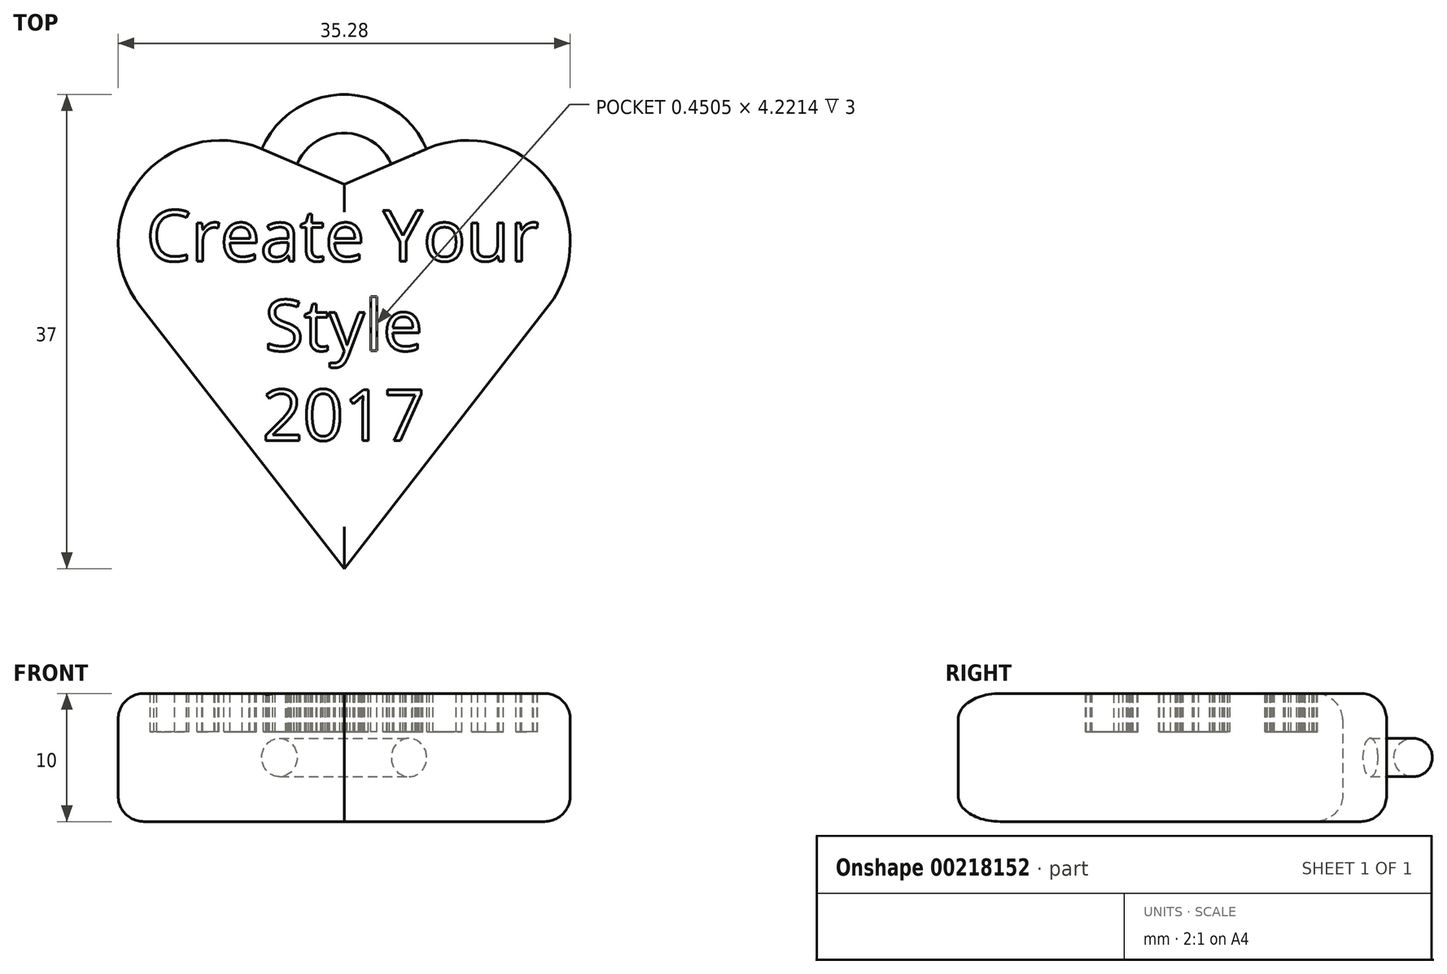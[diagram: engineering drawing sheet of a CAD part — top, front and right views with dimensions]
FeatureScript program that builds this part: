
annotation { "Feature Type Name" : "Feature", "Feature Type Description" : "" }
export const myFeature = defineFeature(function(context is Context, id is Id, definition is map)
    precondition{}
    {
        {
            var Q0;
            Q0=qCreatedBy(makeId("Top.planeOp"),FACE);
            var sketch = newSketch(context, id + "F0", { "sketchPlane" : qUnion([Q0])});
            skLineSegment(sketch, "E0", {"start": v(0, 0) * mm, "end": v(35, 45) * mm});
            skLineSegment(sketch, "E1", {"start": v(35, 45) * mm, "end": v(0, 30) * mm});
            skLineSegment(sketch, "E2.MirrorCS", {"start": v(-35, 45) * mm, "end": v(0, 30) * mm});
            skLineSegment(sketch, "E3.MirrorCS", {"start": v(0, 0) * mm, "end": v(-35, 45) * mm});
            skSolve(sketch);
        }
        {
            var Q0;
            Q0 = qSketchRegion(id + "F0", true);
            extrude(context, id + "F1", {"entities" : qUnion([Q0]), "depth" : 10 * mm, "symmetric" : true});
        }
        {
            var Q0;
            Q0=makeQuery(id+"F1.opExtrude","SWEPT_EDGE",EDGE,{"disambiguationData":[OSD([sQuery(id+"F0.wireOp",EDGE,"E2.MirrorCS"),sQuery(id+"F0.wireOp",EDGE,"E3.MirrorCS")])]});
            var Q1;
            Q1=makeQuery(id+"F1.opExtrude","SWEPT_EDGE",EDGE,{"disambiguationData":[OSD([sQuery(id+"F0.wireOp",EDGE,"E0"),sQuery(id+"F0.wireOp",EDGE,"E1")])]});
            fillet(context, id + "F2", {"entities" : qUnion([Q0, Q1]), "radius" : 8 * mm, "tangentPropagation" : true, "allowEdgeOverflow" : false});
        }
        {
            var Q0;
            Q0=qCreatedBy(makeId("Top.planeOp"),FACE);
            var sketch = newSketch(context, id + "F3", { "sketchPlane" : qUnion([Q0])});
            skCircle(sketch, "E4", {"center": v(0, 30) * mm, "radius": 7 * mm});
            skCircle(sketch, "E5", {"center": v(0, 30) * mm, "radius": 4 * mm});
            skSolve(sketch);
        }
        {
            var Q0;
            Q0=makeQuery(id+"F3.imprint","IMPRINT",FACE,{"disambiguationData":[TD([[makeQuery(id+"F3.imprint","IMPRINT",EDGE,{"derivedFrom":sQuery(id+"F3.wireOp",EDGE,"E4")}),1.0]])]});
            extrude(context, id + "F4", {"entities" : qUnion([Q0]), "operationType" : NewBodyOperationType.ADD, "depth" : 3 * mm, "symmetric" : true});
        }
        {
            var Q0;
            Q0=makeQuery(id+"F4.opExtrude","CAP_EDGE",EDGE,{"disambiguationData":[OSD([sQuery(id+"F3.wireOp",EDGE,"E4")])],"isStart":false});
            var Q1;
            Q1=makeQuery(id+"F4.opExtrude","CAP_EDGE",EDGE,{"disambiguationData":[OSD([sQuery(id+"F3.wireOp",EDGE,"E5")])],"isStart":false});
            var Q2;
            Q2=makeQuery(id+"F4.opExtrude","CAP_EDGE",EDGE,{"disambiguationData":[OSD([sQuery(id+"F3.wireOp",EDGE,"E5")])],"isStart":true});
            var Q3;
            Q3=makeQuery(id+"F4.opExtrude","CAP_EDGE",EDGE,{"disambiguationData":[OSD([sQuery(id+"F3.wireOp",EDGE,"E4")])],"isStart":true});
            fillet(context, id + "F5", {"entities" : qUnion([Q0, Q1, Q2, Q3]), "radius" : 1.5 * mm, "tangentPropagation" : true, "allowEdgeOverflow" : false});
        }
        {
            var Q0;
            Q0=makeQuery(id+"F1.opExtrude","CAP_FACE",FACE,{"disambiguationData":[OSD([sQuery(id+"F0.wireOp",EDGE,"E0"),sQuery(id+"F0.wireOp",EDGE,"E1"),sQuery(id+"F0.wireOp",EDGE,"E2.MirrorCS"),sQuery(id+"F0.wireOp",EDGE,"E3.MirrorCS")])],"isStart":false});
            var sketch = newSketch(context, id + "F6", { "sketchPlane" : qUnion([Q0])});
            skText(sketch, "E6", { "text": "Create Your", "fontName": "OpenSans-Regular.ttf"});
            skText(sketch, "E7", { "text": "Style", "fontName": "OpenSans-Regular.ttf"});
            skText(sketch, "E8", { "text": "2017", "fontName": "OpenSans-Regular.ttf"});
            const initialGuessF6  = {"E6": [-0.01546, 0.024, 1, 0, 0.004], "E7": [-0.0062, 0.017, 1, 0, 0.004], "E8": [-0.0064, 0.01, 1, 0, 0.004]};
            skSetInitialGuess(sketch, initialGuessF6);
            skSolve(sketch);
        }
        {
            var Q0;
            Q0 = qSketchRegion(id + "F6", true);
            extrude(context, id + "F7", {"entities" : qUnion([Q0]), "operationType" : NewBodyOperationType.REMOVE, "oppositeDirection" : true, "depth" : 3 * mm});
        }
        {
            var Q0;
            Q0=makeQuery(id+"F1.opExtrude","CAP_FACE",FACE,{"disambiguationData":[OSD([sQuery(id+"F0.wireOp",EDGE,"E0"),sQuery(id+"F0.wireOp",EDGE,"E1"),sQuery(id+"F0.wireOp",EDGE,"E2.MirrorCS"),sQuery(id+"F0.wireOp",EDGE,"E3.MirrorCS")])],"isStart":true});
            var Q1;
            {var subQ0=sQuery(id+"F0.wireOp",EDGE,"E3.MirrorCS");var subQ1=sQuery(id+"F0.wireOp",EDGE,"E2.MirrorCS");Q1=makeQuery(id+"F2.opFillet","BLEND_EDGE",EDGE,{"blendedFrom":[makeQuery(id+"F1.opExtrude","SWEPT_EDGE",EDGE,{"disambiguationData":[OSD([subQ1,subQ0])]}),makeQuery(id+"F1.opExtrude","CAP_FACE",FACE,{"disambiguationData":[OSD([sQuery(id+"F0.wireOp",EDGE,"E0"),sQuery(id+"F0.wireOp",EDGE,"E1"),subQ1,subQ0])],"isStart":false})],"blendedInto":[makeQuery(id+"F1.opExtrude","CAP_FACE",FACE,{"disambiguationData":[OSD([sQuery(id+"F0.wireOp",EDGE,"E0"),sQuery(id+"F0.wireOp",EDGE,"E1"),subQ1,subQ0])],"isStart":false})]});}
            var Q2;
            Q2=makeQuery(id+"F1.opExtrude","CAP_EDGE",EDGE,{"disambiguationData":[OSD([sQuery(id+"F0.wireOp",EDGE,"E0")])],"isStart":false});
            fillet(context, id + "F8", {"entities" : qUnion([Q0, Q1, Q2]), "radius" : 2 * mm, "tangentPropagation" : true, "allowEdgeOverflow" : false});
        }
    });
